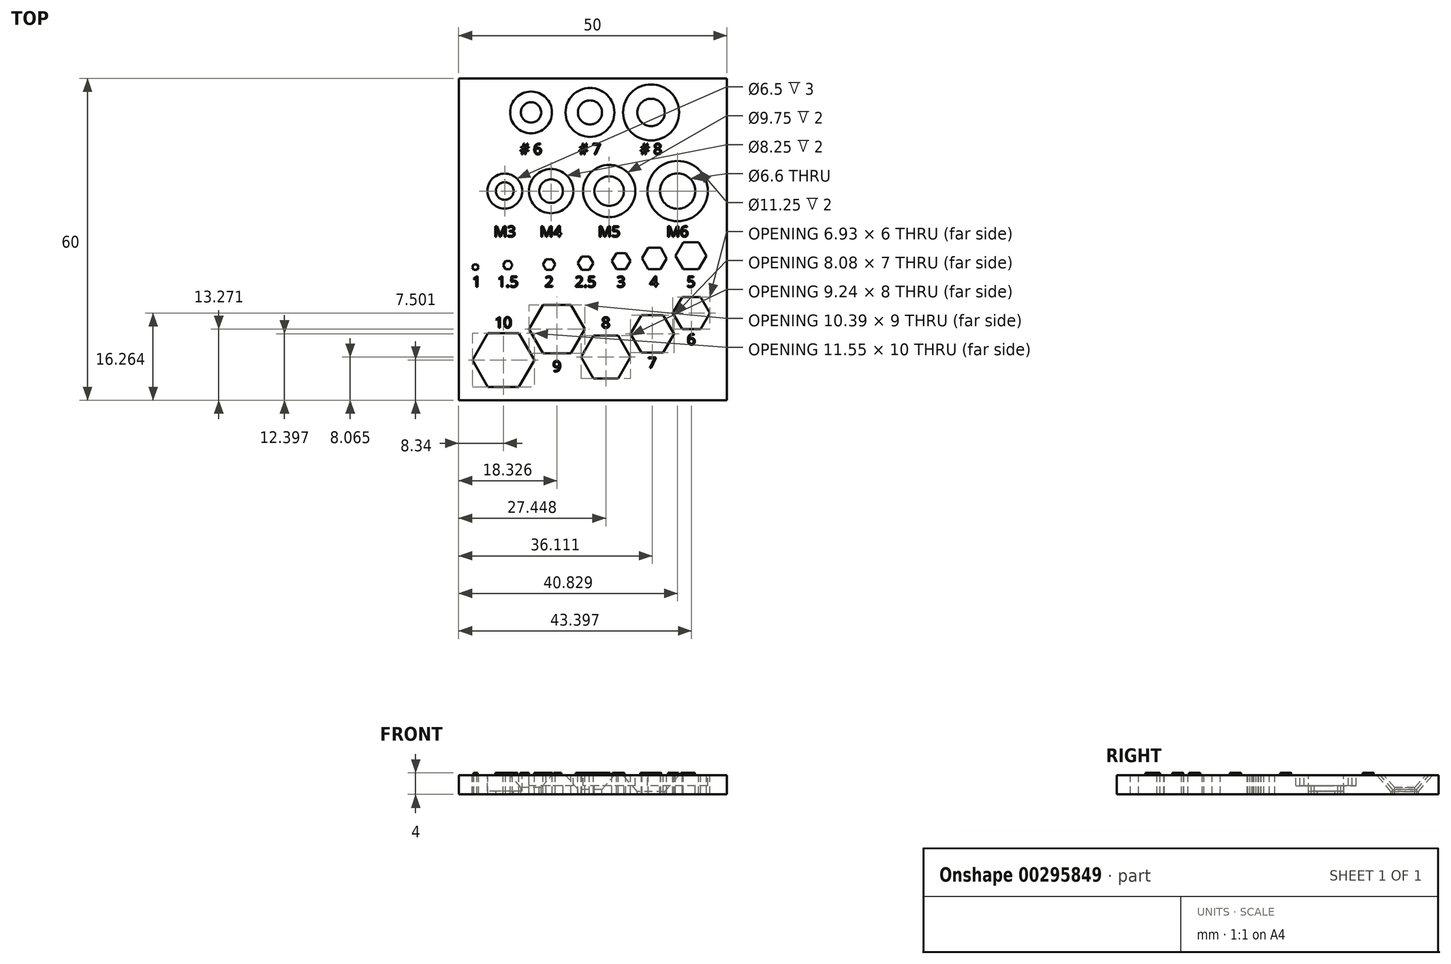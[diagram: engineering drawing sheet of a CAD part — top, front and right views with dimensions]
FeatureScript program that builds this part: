
annotation { "Feature Type Name" : "Feature", "Feature Type Description" : "" }
export const myFeature = defineFeature(function(context is Context, id is Id, definition is map)
    precondition{}
    {
        {
            var Q0;
            Q0=qCreatedBy(makeId("Top.planeOp"),FACE);
            var sketch = newSketch(context, id + "F0", { "sketchPlane" : qUnion([Q0])});
            skPoint(sketch, "E0", {"position": v(-51.98, 21.27) * mm});
            skPoint(sketch, "E1", {"position": v(-43.33, 21.27) * mm});
            skPoint(sketch, "E2", {"position": v(-32.5, 21.27) * mm});
            skPoint(sketch, "E3", {"position": v(-19.74, 21.27) * mm});
            skPoint(sketch, "E4", {"position": v(-47.08, 35.94) * mm});
            skPoint(sketch, "E5", {"position": v(-36.08, 35.94) * mm});
            skPoint(sketch, "E6", {"position": v(-24.7, 35.94) * mm});
            skCircle(sketch, "E7.cCircle", {"center": v(-57.46, 7.08) * mm, "radius": 0.5 * mm, "construction": true});
            skLineSegment(sketch, "E7.0", {"start": v(-57.75, 7.58) * mm, "end": v(-57.17, 7.58) * mm});
            skLineSegment(sketch, "E7.1", {"start": v(-57.17, 7.58) * mm, "end": v(-56.88, 7.08) * mm});
            skLineSegment(sketch, "E7.2", {"start": v(-56.88, 7.08) * mm, "end": v(-57.17, 6.58) * mm});
            skLineSegment(sketch, "E7.3", {"start": v(-57.17, 6.58) * mm, "end": v(-57.75, 6.58) * mm});
            skLineSegment(sketch, "E7.4", {"start": v(-57.75, 6.58) * mm, "end": v(-58.03, 7.08) * mm});
            skLineSegment(sketch, "E7.5", {"start": v(-58.03, 7.08) * mm, "end": v(-57.75, 7.58) * mm});
            skPoint(sketch, "E7.0.midPoint", {"position": v(-57.46, 7.58) * mm});
            skCircle(sketch, "E8.cCircle", {"center": v(-51.4, 7.45) * mm, "radius": 0.75 * mm, "construction": true});
            skLineSegment(sketch, "E8.0", {"start": v(-51.84, 8.2) * mm, "end": v(-50.97, 8.2) * mm});
            skLineSegment(sketch, "E8.1", {"start": v(-50.97, 8.2) * mm, "end": v(-50.54, 7.45) * mm});
            skLineSegment(sketch, "E8.2", {"start": v(-50.54, 7.45) * mm, "end": v(-50.97, 6.7) * mm});
            skLineSegment(sketch, "E8.3", {"start": v(-50.97, 6.7) * mm, "end": v(-51.84, 6.7) * mm});
            skLineSegment(sketch, "E8.4", {"start": v(-51.84, 6.7) * mm, "end": v(-52.27, 7.45) * mm});
            skLineSegment(sketch, "E8.5", {"start": v(-52.27, 7.45) * mm, "end": v(-51.84, 8.2) * mm});
            skPoint(sketch, "E8.0.midPoint", {"position": v(-51.4, 8.2) * mm});
            skCircle(sketch, "E9.cCircle", {"center": v(-43.7, 7.58) * mm, "radius": 1 * mm, "construction": true});
            skLineSegment(sketch, "E9.0", {"start": v(-44.28, 8.58) * mm, "end": v(-43.12, 8.58) * mm});
            skLineSegment(sketch, "E9.1", {"start": v(-43.12, 8.58) * mm, "end": v(-42.55, 7.58) * mm});
            skLineSegment(sketch, "E9.2", {"start": v(-42.55, 7.58) * mm, "end": v(-43.12, 6.58) * mm});
            skLineSegment(sketch, "E9.3", {"start": v(-43.12, 6.58) * mm, "end": v(-44.28, 6.58) * mm});
            skLineSegment(sketch, "E9.4", {"start": v(-44.28, 6.58) * mm, "end": v(-44.86, 7.58) * mm});
            skLineSegment(sketch, "E9.5", {"start": v(-44.86, 7.58) * mm, "end": v(-44.28, 8.58) * mm});
            skPoint(sketch, "E9.0.midPoint", {"position": v(-43.7, 8.58) * mm});
            skCircle(sketch, "E10.cCircle", {"center": v(-36.91, 7.83) * mm, "radius": 1.25 * mm, "construction": true});
            skLineSegment(sketch, "E10.0", {"start": v(-37.63, 9.08) * mm, "end": v(-36.2, 9.08) * mm});
            skLineSegment(sketch, "E10.1", {"start": v(-36.2, 9.08) * mm, "end": v(-35.47, 7.83) * mm});
            skLineSegment(sketch, "E10.2", {"start": v(-35.47, 7.83) * mm, "end": v(-36.2, 6.58) * mm});
            skLineSegment(sketch, "E10.3", {"start": v(-36.2, 6.58) * mm, "end": v(-37.63, 6.58) * mm});
            skLineSegment(sketch, "E10.4", {"start": v(-37.63, 6.58) * mm, "end": v(-38.36, 7.83) * mm});
            skLineSegment(sketch, "E10.5", {"start": v(-38.36, 7.83) * mm, "end": v(-37.63, 9.08) * mm});
            skPoint(sketch, "E10.0.midPoint", {"position": v(-36.91, 9.08) * mm});
            skCircle(sketch, "E11.cCircle", {"center": v(-52.23, -10.23) * mm, "radius": 5 * mm, "construction": true});
            skLineSegment(sketch, "E11.0", {"start": v(-55.12, -5.23) * mm, "end": v(-49.34, -5.23) * mm});
            skLineSegment(sketch, "E11.1", {"start": v(-49.34, -5.23) * mm, "end": v(-46.46, -10.23) * mm});
            skLineSegment(sketch, "E11.2", {"start": v(-46.46, -10.23) * mm, "end": v(-49.34, -15.23) * mm});
            skLineSegment(sketch, "E11.3", {"start": v(-49.34, -15.23) * mm, "end": v(-55.12, -15.23) * mm});
            skLineSegment(sketch, "E11.4", {"start": v(-55.12, -15.23) * mm, "end": v(-58, -10.23) * mm});
            skLineSegment(sketch, "E11.5", {"start": v(-58, -10.23) * mm, "end": v(-55.12, -5.23) * mm});
            skPoint(sketch, "E11.0.midPoint", {"position": v(-52.23, -5.23) * mm});
            skCircle(sketch, "E12.cCircle", {"center": v(-42.24, -4.46) * mm, "radius": 4.5 * mm, "construction": true});
            skLineSegment(sketch, "E12.0", {"start": v(-44.84, 0.04) * mm, "end": v(-39.65, 0.04) * mm});
            skLineSegment(sketch, "E12.1", {"start": v(-39.65, 0.04) * mm, "end": v(-37.05, -4.46) * mm});
            skLineSegment(sketch, "E12.2", {"start": v(-37.05, -4.46) * mm, "end": v(-39.65, -8.96) * mm});
            skLineSegment(sketch, "E12.3", {"start": v(-39.65, -8.96) * mm, "end": v(-44.84, -8.96) * mm});
            skLineSegment(sketch, "E12.4", {"start": v(-44.84, -8.96) * mm, "end": v(-47.44, -4.46) * mm});
            skLineSegment(sketch, "E12.5", {"start": v(-47.44, -4.46) * mm, "end": v(-44.84, 0.04) * mm});
            skPoint(sketch, "E12.0.midPoint", {"position": v(-42.24, 0.04) * mm});
            skCircle(sketch, "E13.cCircle", {"center": v(-33.12, -9.67) * mm, "radius": 4 * mm, "construction": true});
            skLineSegment(sketch, "E13.0", {"start": v(-35.43, -5.67) * mm, "end": v(-30.81, -5.67) * mm});
            skLineSegment(sketch, "E13.1", {"start": v(-30.81, -5.67) * mm, "end": v(-28.5, -9.67) * mm});
            skLineSegment(sketch, "E13.2", {"start": v(-28.5, -9.67) * mm, "end": v(-30.81, -13.67) * mm});
            skLineSegment(sketch, "E13.3", {"start": v(-30.81, -13.67) * mm, "end": v(-35.43, -13.67) * mm});
            skLineSegment(sketch, "E13.4", {"start": v(-35.43, -13.67) * mm, "end": v(-37.74, -9.67) * mm});
            skLineSegment(sketch, "E13.5", {"start": v(-37.74, -9.67) * mm, "end": v(-35.43, -5.67) * mm});
            skPoint(sketch, "E13.0.midPoint", {"position": v(-33.12, -5.67) * mm});
            skCircle(sketch, "E14.cCircle", {"center": v(-24.46, -5.33) * mm, "radius": 3.5 * mm, "construction": true});
            skLineSegment(sketch, "E14.0", {"start": v(-26.48, -1.83) * mm, "end": v(-22.44, -1.83) * mm});
            skLineSegment(sketch, "E14.1", {"start": v(-22.44, -1.83) * mm, "end": v(-20.42, -5.33) * mm});
            skLineSegment(sketch, "E14.2", {"start": v(-20.42, -5.33) * mm, "end": v(-22.44, -8.83) * mm});
            skLineSegment(sketch, "E14.3", {"start": v(-22.44, -8.83) * mm, "end": v(-26.48, -8.83) * mm});
            skLineSegment(sketch, "E14.4", {"start": v(-26.48, -8.83) * mm, "end": v(-28.5, -5.33) * mm});
            skLineSegment(sketch, "E14.5", {"start": v(-28.5, -5.33) * mm, "end": v(-26.48, -1.83) * mm});
            skPoint(sketch, "E14.0.midPoint", {"position": v(-24.46, -1.83) * mm});
            skCircle(sketch, "E15.cCircle", {"center": v(-17.17, -1.47) * mm, "radius": 3 * mm, "construction": true});
            skLineSegment(sketch, "E15.0", {"start": v(-18.9, 1.53) * mm, "end": v(-15.44, 1.53) * mm});
            skLineSegment(sketch, "E15.1", {"start": v(-15.44, 1.53) * mm, "end": v(-13.7, -1.47) * mm});
            skLineSegment(sketch, "E15.2", {"start": v(-13.7, -1.47) * mm, "end": v(-15.44, -4.47) * mm});
            skLineSegment(sketch, "E15.3", {"start": v(-15.44, -4.47) * mm, "end": v(-18.9, -4.47) * mm});
            skLineSegment(sketch, "E15.4", {"start": v(-18.9, -4.47) * mm, "end": v(-20.64, -1.47) * mm});
            skLineSegment(sketch, "E15.5", {"start": v(-20.64, -1.47) * mm, "end": v(-18.9, 1.53) * mm});
            skPoint(sketch, "E15.0.midPoint", {"position": v(-17.17, 1.53) * mm});
            skCircle(sketch, "E16.cCircle", {"center": v(-30.3, 8.2) * mm, "radius": 1.5 * mm, "construction": true});
            skLineSegment(sketch, "E16.0", {"start": v(-31.16, 9.7) * mm, "end": v(-29.43, 9.7) * mm});
            skLineSegment(sketch, "E16.1", {"start": v(-29.43, 9.7) * mm, "end": v(-28.56, 8.2) * mm});
            skLineSegment(sketch, "E16.2", {"start": v(-28.56, 8.2) * mm, "end": v(-29.43, 6.7) * mm});
            skLineSegment(sketch, "E16.3", {"start": v(-29.43, 6.7) * mm, "end": v(-31.16, 6.7) * mm});
            skLineSegment(sketch, "E16.4", {"start": v(-31.16, 6.7) * mm, "end": v(-32.02, 8.2) * mm});
            skLineSegment(sketch, "E16.5", {"start": v(-32.02, 8.2) * mm, "end": v(-31.16, 9.7) * mm});
            skPoint(sketch, "E16.0.midPoint", {"position": v(-30.3, 9.7) * mm});
            skCircle(sketch, "E17.cCircle", {"center": v(-24.08, 8.7) * mm, "radius": 2 * mm, "construction": true});
            skLineSegment(sketch, "E17.0", {"start": v(-25.22, 10.72) * mm, "end": v(-22.9, 10.7) * mm});
            skLineSegment(sketch, "E17.1", {"start": v(-22.9, 10.7) * mm, "end": v(-21.77, 8.68) * mm});
            skLineSegment(sketch, "E17.2", {"start": v(-21.77, 8.68) * mm, "end": v(-22.94, 6.7) * mm});
            skLineSegment(sketch, "E17.3", {"start": v(-22.94, 6.7) * mm, "end": v(-25.25, 6.72) * mm});
            skLineSegment(sketch, "E17.4", {"start": v(-25.25, 6.72) * mm, "end": v(-26.39, 8.73) * mm});
            skLineSegment(sketch, "E17.5", {"start": v(-26.39, 8.73) * mm, "end": v(-25.22, 10.72) * mm});
            skPoint(sketch, "E17.0.midPoint", {"position": v(-24.06, 10.7) * mm});
            skCircle(sketch, "E18.cCircle", {"center": v(-17.25, 9.2) * mm, "radius": 2.5 * mm, "construction": true});
            skLineSegment(sketch, "E18.0", {"start": v(-18.7, 11.7) * mm, "end": v(-15.8, 11.7) * mm});
            skLineSegment(sketch, "E18.1", {"start": v(-15.8, 11.7) * mm, "end": v(-14.36, 9.2) * mm});
            skLineSegment(sketch, "E18.2", {"start": v(-14.36, 9.2) * mm, "end": v(-15.8, 6.7) * mm});
            skLineSegment(sketch, "E18.3", {"start": v(-15.8, 6.7) * mm, "end": v(-18.7, 6.7) * mm});
            skLineSegment(sketch, "E18.4", {"start": v(-18.7, 6.7) * mm, "end": v(-20.13, 9.2) * mm});
            skLineSegment(sketch, "E18.5", {"start": v(-20.13, 9.2) * mm, "end": v(-18.7, 11.7) * mm});
            skPoint(sketch, "E18.0.midPoint", {"position": v(-17.25, 11.7) * mm});
            skLineSegment(sketch, "E19.bottom", {"start": v(-60.57, -17.73) * mm, "end": v(-10.57, -17.73) * mm});
            skLineSegment(sketch, "E19.top", {"start": v(-60.57, 42.27) * mm, "end": v(-10.57, 42.27) * mm});
            skLineSegment(sketch, "E19.left", {"start": v(-60.57, -17.73) * mm, "end": v(-60.57, 42.27) * mm});
            skLineSegment(sketch, "E19.right", {"start": v(-10.57, -17.73) * mm, "end": v(-10.57, 42.27) * mm});
            skSolve(sketch);
        }
        {
            var Q0;
            Q0=makeQuery(id+"F0.imprint","IMPRINT",FACE,{"disambiguationData":[TD([[makeQuery(id+"F0.imprint","IMPRINT",EDGE,{"derivedFrom":sQuery(id+"F0.wireOp",EDGE,"E7.0")}),1.0]])]});
            extrude(context, id + "F1", {"entities" : qUnion([Q0]), "oppositeDirection" : true, "depth" : 3.6 * mm});
        }
        {
            var Q0;
            Q0=sQuery(id+"F0.wireOp",VERTEX,"E0");
            var Q1;
            Q1=makeQuery(id+"F1.opExtrude","SWEPT_BODY",BODY,{"disambiguationData":[OSD([sQuery(id+"F0.wireOp",EDGE,"E7.0"),sQuery(id+"F0.wireOp",EDGE,"E7.1"),sQuery(id+"F0.wireOp",EDGE,"E7.2"),sQuery(id+"F0.wireOp",EDGE,"E7.3"),sQuery(id+"F0.wireOp",EDGE,"E7.4"),sQuery(id+"F0.wireOp",EDGE,"E7.5"),sQuery(id+"F0.wireOp",EDGE,"E8.0"),sQuery(id+"F0.wireOp",EDGE,"E8.1"),sQuery(id+"F0.wireOp",EDGE,"E8.2"),sQuery(id+"F0.wireOp",EDGE,"E8.3"),sQuery(id+"F0.wireOp",EDGE,"E8.4"),sQuery(id+"F0.wireOp",EDGE,"E8.5"),sQuery(id+"F0.wireOp",EDGE,"E9.0"),sQuery(id+"F0.wireOp",EDGE,"E9.1"),sQuery(id+"F0.wireOp",EDGE,"E9.2"),sQuery(id+"F0.wireOp",EDGE,"E9.3"),sQuery(id+"F0.wireOp",EDGE,"E9.4"),sQuery(id+"F0.wireOp",EDGE,"E9.5"),sQuery(id+"F0.wireOp",EDGE,"E10.0"),sQuery(id+"F0.wireOp",EDGE,"E10.1"),sQuery(id+"F0.wireOp",EDGE,"E10.2"),sQuery(id+"F0.wireOp",EDGE,"E10.3"),sQuery(id+"F0.wireOp",EDGE,"E10.4"),sQuery(id+"F0.wireOp",EDGE,"E10.5"),sQuery(id+"F0.wireOp",EDGE,"E11.0"),sQuery(id+"F0.wireOp",EDGE,"E11.1"),sQuery(id+"F0.wireOp",EDGE,"E11.2"),sQuery(id+"F0.wireOp",EDGE,"E11.3"),sQuery(id+"F0.wireOp",EDGE,"E11.4"),sQuery(id+"F0.wireOp",EDGE,"E11.5"),sQuery(id+"F0.wireOp",EDGE,"E12.0"),sQuery(id+"F0.wireOp",EDGE,"E12.1"),sQuery(id+"F0.wireOp",EDGE,"E12.2"),sQuery(id+"F0.wireOp",EDGE,"E12.3"),sQuery(id+"F0.wireOp",EDGE,"E12.4"),sQuery(id+"F0.wireOp",EDGE,"E12.5"),sQuery(id+"F0.wireOp",EDGE,"E13.0"),sQuery(id+"F0.wireOp",EDGE,"E13.1"),sQuery(id+"F0.wireOp",EDGE,"E13.2"),sQuery(id+"F0.wireOp",EDGE,"E13.3"),sQuery(id+"F0.wireOp",EDGE,"E13.4"),sQuery(id+"F0.wireOp",EDGE,"E13.5"),sQuery(id+"F0.wireOp",EDGE,"E14.0"),sQuery(id+"F0.wireOp",EDGE,"E14.1"),sQuery(id+"F0.wireOp",EDGE,"E14.2"),sQuery(id+"F0.wireOp",EDGE,"E14.3"),sQuery(id+"F0.wireOp",EDGE,"E14.4"),sQuery(id+"F0.wireOp",EDGE,"E14.5"),sQuery(id+"F0.wireOp",EDGE,"E15.0"),sQuery(id+"F0.wireOp",EDGE,"E15.1"),sQuery(id+"F0.wireOp",EDGE,"E15.2"),sQuery(id+"F0.wireOp",EDGE,"E15.3"),sQuery(id+"F0.wireOp",EDGE,"E15.4"),sQuery(id+"F0.wireOp",EDGE,"E15.5"),sQuery(id+"F0.wireOp",EDGE,"E16.0"),sQuery(id+"F0.wireOp",EDGE,"E16.1"),sQuery(id+"F0.wireOp",EDGE,"E16.2"),sQuery(id+"F0.wireOp",EDGE,"E16.3"),sQuery(id+"F0.wireOp",EDGE,"E16.4"),sQuery(id+"F0.wireOp",EDGE,"E16.5"),sQuery(id+"F0.wireOp",EDGE,"E17.0"),sQuery(id+"F0.wireOp",EDGE,"E17.1"),sQuery(id+"F0.wireOp",EDGE,"E17.2"),sQuery(id+"F0.wireOp",EDGE,"E17.3"),sQuery(id+"F0.wireOp",EDGE,"E17.4"),sQuery(id+"F0.wireOp",EDGE,"E17.5"),sQuery(id+"F0.wireOp",EDGE,"E18.0"),sQuery(id+"F0.wireOp",EDGE,"E18.1"),sQuery(id+"F0.wireOp",EDGE,"E18.2"),sQuery(id+"F0.wireOp",EDGE,"E18.3"),sQuery(id+"F0.wireOp",EDGE,"E18.4"),sQuery(id+"F0.wireOp",EDGE,"E18.5"),sQuery(id+"F0.wireOp",EDGE,"E19.bottom"),sQuery(id+"F0.wireOp",EDGE,"E19.top"),sQuery(id+"F0.wireOp",EDGE,"E19.left"),sQuery(id+"F0.wireOp",EDGE,"E19.right")])]});
            hole(context, id + "F2", {"style" : HoleStyle.C_BORE, "endStyle" : HoleEndStyle.THROUGH, "standardTappedOrClearance" : lookupTablePath({ "standard" : "ISO", "fit" : "Normal", "size" : "M3", "type" : "Clearance" }), "standardBlindInLast" : lookupTablePath({ "fit" : "Standard", "standard" : "ISO", "size" : "M3", "type" : "Clearance" }), "holeDiameter" : 3.3 * mm, "cBoreDiameter" : 6.5 * mm, "cBoreDepth" : 3 * mm, "tappedDepth" : 12.7 * mm, "tapClearance" : 3, "locations" : qUnion([Q0]), "scope" : qUnion([Q1])});
        }
        {
            var Q0;
            Q0=sQuery(id+"F0.wireOp",VERTEX,"E2");
            var Q1;
            Q1=makeQuery(id+"F1.opExtrude","SWEPT_BODY",BODY,{"disambiguationData":[OSD([sQuery(id+"F0.wireOp",EDGE,"E7.0"),sQuery(id+"F0.wireOp",EDGE,"E7.1"),sQuery(id+"F0.wireOp",EDGE,"E7.2"),sQuery(id+"F0.wireOp",EDGE,"E7.3"),sQuery(id+"F0.wireOp",EDGE,"E7.4"),sQuery(id+"F0.wireOp",EDGE,"E7.5"),sQuery(id+"F0.wireOp",EDGE,"E8.0"),sQuery(id+"F0.wireOp",EDGE,"E8.1"),sQuery(id+"F0.wireOp",EDGE,"E8.2"),sQuery(id+"F0.wireOp",EDGE,"E8.3"),sQuery(id+"F0.wireOp",EDGE,"E8.4"),sQuery(id+"F0.wireOp",EDGE,"E8.5"),sQuery(id+"F0.wireOp",EDGE,"E9.0"),sQuery(id+"F0.wireOp",EDGE,"E9.1"),sQuery(id+"F0.wireOp",EDGE,"E9.2"),sQuery(id+"F0.wireOp",EDGE,"E9.3"),sQuery(id+"F0.wireOp",EDGE,"E9.4"),sQuery(id+"F0.wireOp",EDGE,"E9.5"),sQuery(id+"F0.wireOp",EDGE,"E10.0"),sQuery(id+"F0.wireOp",EDGE,"E10.1"),sQuery(id+"F0.wireOp",EDGE,"E10.2"),sQuery(id+"F0.wireOp",EDGE,"E10.3"),sQuery(id+"F0.wireOp",EDGE,"E10.4"),sQuery(id+"F0.wireOp",EDGE,"E10.5"),sQuery(id+"F0.wireOp",EDGE,"E11.0"),sQuery(id+"F0.wireOp",EDGE,"E11.1"),sQuery(id+"F0.wireOp",EDGE,"E11.2"),sQuery(id+"F0.wireOp",EDGE,"E11.3"),sQuery(id+"F0.wireOp",EDGE,"E11.4"),sQuery(id+"F0.wireOp",EDGE,"E11.5"),sQuery(id+"F0.wireOp",EDGE,"E12.0"),sQuery(id+"F0.wireOp",EDGE,"E12.1"),sQuery(id+"F0.wireOp",EDGE,"E12.2"),sQuery(id+"F0.wireOp",EDGE,"E12.3"),sQuery(id+"F0.wireOp",EDGE,"E12.4"),sQuery(id+"F0.wireOp",EDGE,"E12.5"),sQuery(id+"F0.wireOp",EDGE,"E13.0"),sQuery(id+"F0.wireOp",EDGE,"E13.1"),sQuery(id+"F0.wireOp",EDGE,"E13.2"),sQuery(id+"F0.wireOp",EDGE,"E13.3"),sQuery(id+"F0.wireOp",EDGE,"E13.4"),sQuery(id+"F0.wireOp",EDGE,"E13.5"),sQuery(id+"F0.wireOp",EDGE,"E14.0"),sQuery(id+"F0.wireOp",EDGE,"E14.1"),sQuery(id+"F0.wireOp",EDGE,"E14.2"),sQuery(id+"F0.wireOp",EDGE,"E14.3"),sQuery(id+"F0.wireOp",EDGE,"E14.4"),sQuery(id+"F0.wireOp",EDGE,"E14.5"),sQuery(id+"F0.wireOp",EDGE,"E15.0"),sQuery(id+"F0.wireOp",EDGE,"E15.1"),sQuery(id+"F0.wireOp",EDGE,"E15.2"),sQuery(id+"F0.wireOp",EDGE,"E15.3"),sQuery(id+"F0.wireOp",EDGE,"E15.4"),sQuery(id+"F0.wireOp",EDGE,"E15.5"),sQuery(id+"F0.wireOp",EDGE,"E16.0"),sQuery(id+"F0.wireOp",EDGE,"E16.1"),sQuery(id+"F0.wireOp",EDGE,"E16.2"),sQuery(id+"F0.wireOp",EDGE,"E16.3"),sQuery(id+"F0.wireOp",EDGE,"E16.4"),sQuery(id+"F0.wireOp",EDGE,"E16.5"),sQuery(id+"F0.wireOp",EDGE,"E17.0"),sQuery(id+"F0.wireOp",EDGE,"E17.1"),sQuery(id+"F0.wireOp",EDGE,"E17.2"),sQuery(id+"F0.wireOp",EDGE,"E17.3"),sQuery(id+"F0.wireOp",EDGE,"E17.4"),sQuery(id+"F0.wireOp",EDGE,"E17.5"),sQuery(id+"F0.wireOp",EDGE,"E18.0"),sQuery(id+"F0.wireOp",EDGE,"E18.1"),sQuery(id+"F0.wireOp",EDGE,"E18.2"),sQuery(id+"F0.wireOp",EDGE,"E18.3"),sQuery(id+"F0.wireOp",EDGE,"E18.4"),sQuery(id+"F0.wireOp",EDGE,"E18.5"),sQuery(id+"F0.wireOp",EDGE,"E19.bottom"),sQuery(id+"F0.wireOp",EDGE,"E19.top"),sQuery(id+"F0.wireOp",EDGE,"E19.left"),sQuery(id+"F0.wireOp",EDGE,"E19.right")])]});
            hole(context, id + "F3", {"style" : HoleStyle.C_BORE, "endStyle" : HoleEndStyle.THROUGH, "holeDiameter" : 5.5 * mm, "cBoreDiameter" : 9.75 * mm, "cBoreDepth" : 2 * mm, "tappedDepth" : 12.7 * mm, "tapClearance" : 3, "locations" : qUnion([Q0]), "scope" : qUnion([Q1])});
        }
        {
            var Q0;
            Q0=sQuery(id+"F0.wireOp",VERTEX,"E1");
            var Q1;
            Q1=makeQuery(id+"F1.opExtrude","SWEPT_BODY",BODY,{"disambiguationData":[OSD([sQuery(id+"F0.wireOp",EDGE,"E7.0"),sQuery(id+"F0.wireOp",EDGE,"E7.1"),sQuery(id+"F0.wireOp",EDGE,"E7.2"),sQuery(id+"F0.wireOp",EDGE,"E7.3"),sQuery(id+"F0.wireOp",EDGE,"E7.4"),sQuery(id+"F0.wireOp",EDGE,"E7.5"),sQuery(id+"F0.wireOp",EDGE,"E8.0"),sQuery(id+"F0.wireOp",EDGE,"E8.1"),sQuery(id+"F0.wireOp",EDGE,"E8.2"),sQuery(id+"F0.wireOp",EDGE,"E8.3"),sQuery(id+"F0.wireOp",EDGE,"E8.4"),sQuery(id+"F0.wireOp",EDGE,"E8.5"),sQuery(id+"F0.wireOp",EDGE,"E9.0"),sQuery(id+"F0.wireOp",EDGE,"E9.1"),sQuery(id+"F0.wireOp",EDGE,"E9.2"),sQuery(id+"F0.wireOp",EDGE,"E9.3"),sQuery(id+"F0.wireOp",EDGE,"E9.4"),sQuery(id+"F0.wireOp",EDGE,"E9.5"),sQuery(id+"F0.wireOp",EDGE,"E10.0"),sQuery(id+"F0.wireOp",EDGE,"E10.1"),sQuery(id+"F0.wireOp",EDGE,"E10.2"),sQuery(id+"F0.wireOp",EDGE,"E10.3"),sQuery(id+"F0.wireOp",EDGE,"E10.4"),sQuery(id+"F0.wireOp",EDGE,"E10.5"),sQuery(id+"F0.wireOp",EDGE,"E11.0"),sQuery(id+"F0.wireOp",EDGE,"E11.1"),sQuery(id+"F0.wireOp",EDGE,"E11.2"),sQuery(id+"F0.wireOp",EDGE,"E11.3"),sQuery(id+"F0.wireOp",EDGE,"E11.4"),sQuery(id+"F0.wireOp",EDGE,"E11.5"),sQuery(id+"F0.wireOp",EDGE,"E12.0"),sQuery(id+"F0.wireOp",EDGE,"E12.1"),sQuery(id+"F0.wireOp",EDGE,"E12.2"),sQuery(id+"F0.wireOp",EDGE,"E12.3"),sQuery(id+"F0.wireOp",EDGE,"E12.4"),sQuery(id+"F0.wireOp",EDGE,"E12.5"),sQuery(id+"F0.wireOp",EDGE,"E13.0"),sQuery(id+"F0.wireOp",EDGE,"E13.1"),sQuery(id+"F0.wireOp",EDGE,"E13.2"),sQuery(id+"F0.wireOp",EDGE,"E13.3"),sQuery(id+"F0.wireOp",EDGE,"E13.4"),sQuery(id+"F0.wireOp",EDGE,"E13.5"),sQuery(id+"F0.wireOp",EDGE,"E14.0"),sQuery(id+"F0.wireOp",EDGE,"E14.1"),sQuery(id+"F0.wireOp",EDGE,"E14.2"),sQuery(id+"F0.wireOp",EDGE,"E14.3"),sQuery(id+"F0.wireOp",EDGE,"E14.4"),sQuery(id+"F0.wireOp",EDGE,"E14.5"),sQuery(id+"F0.wireOp",EDGE,"E15.0"),sQuery(id+"F0.wireOp",EDGE,"E15.1"),sQuery(id+"F0.wireOp",EDGE,"E15.2"),sQuery(id+"F0.wireOp",EDGE,"E15.3"),sQuery(id+"F0.wireOp",EDGE,"E15.4"),sQuery(id+"F0.wireOp",EDGE,"E15.5"),sQuery(id+"F0.wireOp",EDGE,"E16.0"),sQuery(id+"F0.wireOp",EDGE,"E16.1"),sQuery(id+"F0.wireOp",EDGE,"E16.2"),sQuery(id+"F0.wireOp",EDGE,"E16.3"),sQuery(id+"F0.wireOp",EDGE,"E16.4"),sQuery(id+"F0.wireOp",EDGE,"E16.5"),sQuery(id+"F0.wireOp",EDGE,"E17.0"),sQuery(id+"F0.wireOp",EDGE,"E17.1"),sQuery(id+"F0.wireOp",EDGE,"E17.2"),sQuery(id+"F0.wireOp",EDGE,"E17.3"),sQuery(id+"F0.wireOp",EDGE,"E17.4"),sQuery(id+"F0.wireOp",EDGE,"E17.5"),sQuery(id+"F0.wireOp",EDGE,"E18.0"),sQuery(id+"F0.wireOp",EDGE,"E18.1"),sQuery(id+"F0.wireOp",EDGE,"E18.2"),sQuery(id+"F0.wireOp",EDGE,"E18.3"),sQuery(id+"F0.wireOp",EDGE,"E18.4"),sQuery(id+"F0.wireOp",EDGE,"E18.5"),sQuery(id+"F0.wireOp",EDGE,"E19.bottom"),sQuery(id+"F0.wireOp",EDGE,"E19.top"),sQuery(id+"F0.wireOp",EDGE,"E19.left"),sQuery(id+"F0.wireOp",EDGE,"E19.right")])]});
            hole(context, id + "F4", {"style" : HoleStyle.C_BORE, "endStyle" : HoleEndStyle.THROUGH, "holeDiameter" : 4.4 * mm, "cBoreDiameter" : 8.25 * mm, "cBoreDepth" : 2 * mm, "tappedDepth" : 12.7 * mm, "tapClearance" : 3, "locations" : qUnion([Q0]), "scope" : qUnion([Q1])});
        }
        {
            var Q0;
            Q0=sQuery(id+"F0.wireOp",VERTEX,"E3");
            var Q1;
            Q1=makeQuery(id+"F1.opExtrude","SWEPT_BODY",BODY,{"disambiguationData":[OSD([sQuery(id+"F0.wireOp",EDGE,"E7.0"),sQuery(id+"F0.wireOp",EDGE,"E7.1"),sQuery(id+"F0.wireOp",EDGE,"E7.2"),sQuery(id+"F0.wireOp",EDGE,"E7.3"),sQuery(id+"F0.wireOp",EDGE,"E7.4"),sQuery(id+"F0.wireOp",EDGE,"E7.5"),sQuery(id+"F0.wireOp",EDGE,"E8.0"),sQuery(id+"F0.wireOp",EDGE,"E8.1"),sQuery(id+"F0.wireOp",EDGE,"E8.2"),sQuery(id+"F0.wireOp",EDGE,"E8.3"),sQuery(id+"F0.wireOp",EDGE,"E8.4"),sQuery(id+"F0.wireOp",EDGE,"E8.5"),sQuery(id+"F0.wireOp",EDGE,"E9.0"),sQuery(id+"F0.wireOp",EDGE,"E9.1"),sQuery(id+"F0.wireOp",EDGE,"E9.2"),sQuery(id+"F0.wireOp",EDGE,"E9.3"),sQuery(id+"F0.wireOp",EDGE,"E9.4"),sQuery(id+"F0.wireOp",EDGE,"E9.5"),sQuery(id+"F0.wireOp",EDGE,"E10.0"),sQuery(id+"F0.wireOp",EDGE,"E10.1"),sQuery(id+"F0.wireOp",EDGE,"E10.2"),sQuery(id+"F0.wireOp",EDGE,"E10.3"),sQuery(id+"F0.wireOp",EDGE,"E10.4"),sQuery(id+"F0.wireOp",EDGE,"E10.5"),sQuery(id+"F0.wireOp",EDGE,"E11.0"),sQuery(id+"F0.wireOp",EDGE,"E11.1"),sQuery(id+"F0.wireOp",EDGE,"E11.2"),sQuery(id+"F0.wireOp",EDGE,"E11.3"),sQuery(id+"F0.wireOp",EDGE,"E11.4"),sQuery(id+"F0.wireOp",EDGE,"E11.5"),sQuery(id+"F0.wireOp",EDGE,"E12.0"),sQuery(id+"F0.wireOp",EDGE,"E12.1"),sQuery(id+"F0.wireOp",EDGE,"E12.2"),sQuery(id+"F0.wireOp",EDGE,"E12.3"),sQuery(id+"F0.wireOp",EDGE,"E12.4"),sQuery(id+"F0.wireOp",EDGE,"E12.5"),sQuery(id+"F0.wireOp",EDGE,"E13.0"),sQuery(id+"F0.wireOp",EDGE,"E13.1"),sQuery(id+"F0.wireOp",EDGE,"E13.2"),sQuery(id+"F0.wireOp",EDGE,"E13.3"),sQuery(id+"F0.wireOp",EDGE,"E13.4"),sQuery(id+"F0.wireOp",EDGE,"E13.5"),sQuery(id+"F0.wireOp",EDGE,"E14.0"),sQuery(id+"F0.wireOp",EDGE,"E14.1"),sQuery(id+"F0.wireOp",EDGE,"E14.2"),sQuery(id+"F0.wireOp",EDGE,"E14.3"),sQuery(id+"F0.wireOp",EDGE,"E14.4"),sQuery(id+"F0.wireOp",EDGE,"E14.5"),sQuery(id+"F0.wireOp",EDGE,"E15.0"),sQuery(id+"F0.wireOp",EDGE,"E15.1"),sQuery(id+"F0.wireOp",EDGE,"E15.2"),sQuery(id+"F0.wireOp",EDGE,"E15.3"),sQuery(id+"F0.wireOp",EDGE,"E15.4"),sQuery(id+"F0.wireOp",EDGE,"E15.5"),sQuery(id+"F0.wireOp",EDGE,"E16.0"),sQuery(id+"F0.wireOp",EDGE,"E16.1"),sQuery(id+"F0.wireOp",EDGE,"E16.2"),sQuery(id+"F0.wireOp",EDGE,"E16.3"),sQuery(id+"F0.wireOp",EDGE,"E16.4"),sQuery(id+"F0.wireOp",EDGE,"E16.5"),sQuery(id+"F0.wireOp",EDGE,"E17.0"),sQuery(id+"F0.wireOp",EDGE,"E17.1"),sQuery(id+"F0.wireOp",EDGE,"E17.2"),sQuery(id+"F0.wireOp",EDGE,"E17.3"),sQuery(id+"F0.wireOp",EDGE,"E17.4"),sQuery(id+"F0.wireOp",EDGE,"E17.5"),sQuery(id+"F0.wireOp",EDGE,"E18.0"),sQuery(id+"F0.wireOp",EDGE,"E18.1"),sQuery(id+"F0.wireOp",EDGE,"E18.2"),sQuery(id+"F0.wireOp",EDGE,"E18.3"),sQuery(id+"F0.wireOp",EDGE,"E18.4"),sQuery(id+"F0.wireOp",EDGE,"E18.5"),sQuery(id+"F0.wireOp",EDGE,"E19.bottom"),sQuery(id+"F0.wireOp",EDGE,"E19.top"),sQuery(id+"F0.wireOp",EDGE,"E19.left"),sQuery(id+"F0.wireOp",EDGE,"E19.right")])]});
            hole(context, id + "F5", {"style" : HoleStyle.C_BORE, "endStyle" : HoleEndStyle.THROUGH, "holeDiameter" : 6.6 * mm, "cBoreDiameter" : 11.25 * mm, "cBoreDepth" : 2 * mm, "tappedDepth" : 12.7 * mm, "tapClearance" : 3, "locations" : qUnion([Q0]), "scope" : qUnion([Q1])});
        }
        {
            var Q0;
            Q0=sQuery(id+"F0.wireOp",VERTEX,"E4");
            var Q1;
            Q1=makeQuery(id+"F1.opExtrude","SWEPT_BODY",BODY,{"disambiguationData":[OSD([sQuery(id+"F0.wireOp",EDGE,"E7.0"),sQuery(id+"F0.wireOp",EDGE,"E7.1"),sQuery(id+"F0.wireOp",EDGE,"E7.2"),sQuery(id+"F0.wireOp",EDGE,"E7.3"),sQuery(id+"F0.wireOp",EDGE,"E7.4"),sQuery(id+"F0.wireOp",EDGE,"E7.5"),sQuery(id+"F0.wireOp",EDGE,"E8.0"),sQuery(id+"F0.wireOp",EDGE,"E8.1"),sQuery(id+"F0.wireOp",EDGE,"E8.2"),sQuery(id+"F0.wireOp",EDGE,"E8.3"),sQuery(id+"F0.wireOp",EDGE,"E8.4"),sQuery(id+"F0.wireOp",EDGE,"E8.5"),sQuery(id+"F0.wireOp",EDGE,"E9.0"),sQuery(id+"F0.wireOp",EDGE,"E9.1"),sQuery(id+"F0.wireOp",EDGE,"E9.2"),sQuery(id+"F0.wireOp",EDGE,"E9.3"),sQuery(id+"F0.wireOp",EDGE,"E9.4"),sQuery(id+"F0.wireOp",EDGE,"E9.5"),sQuery(id+"F0.wireOp",EDGE,"E10.0"),sQuery(id+"F0.wireOp",EDGE,"E10.1"),sQuery(id+"F0.wireOp",EDGE,"E10.2"),sQuery(id+"F0.wireOp",EDGE,"E10.3"),sQuery(id+"F0.wireOp",EDGE,"E10.4"),sQuery(id+"F0.wireOp",EDGE,"E10.5"),sQuery(id+"F0.wireOp",EDGE,"E11.0"),sQuery(id+"F0.wireOp",EDGE,"E11.1"),sQuery(id+"F0.wireOp",EDGE,"E11.2"),sQuery(id+"F0.wireOp",EDGE,"E11.3"),sQuery(id+"F0.wireOp",EDGE,"E11.4"),sQuery(id+"F0.wireOp",EDGE,"E11.5"),sQuery(id+"F0.wireOp",EDGE,"E12.0"),sQuery(id+"F0.wireOp",EDGE,"E12.1"),sQuery(id+"F0.wireOp",EDGE,"E12.2"),sQuery(id+"F0.wireOp",EDGE,"E12.3"),sQuery(id+"F0.wireOp",EDGE,"E12.4"),sQuery(id+"F0.wireOp",EDGE,"E12.5"),sQuery(id+"F0.wireOp",EDGE,"E13.0"),sQuery(id+"F0.wireOp",EDGE,"E13.1"),sQuery(id+"F0.wireOp",EDGE,"E13.2"),sQuery(id+"F0.wireOp",EDGE,"E13.3"),sQuery(id+"F0.wireOp",EDGE,"E13.4"),sQuery(id+"F0.wireOp",EDGE,"E13.5"),sQuery(id+"F0.wireOp",EDGE,"E14.0"),sQuery(id+"F0.wireOp",EDGE,"E14.1"),sQuery(id+"F0.wireOp",EDGE,"E14.2"),sQuery(id+"F0.wireOp",EDGE,"E14.3"),sQuery(id+"F0.wireOp",EDGE,"E14.4"),sQuery(id+"F0.wireOp",EDGE,"E14.5"),sQuery(id+"F0.wireOp",EDGE,"E15.0"),sQuery(id+"F0.wireOp",EDGE,"E15.1"),sQuery(id+"F0.wireOp",EDGE,"E15.2"),sQuery(id+"F0.wireOp",EDGE,"E15.3"),sQuery(id+"F0.wireOp",EDGE,"E15.4"),sQuery(id+"F0.wireOp",EDGE,"E15.5"),sQuery(id+"F0.wireOp",EDGE,"E16.0"),sQuery(id+"F0.wireOp",EDGE,"E16.1"),sQuery(id+"F0.wireOp",EDGE,"E16.2"),sQuery(id+"F0.wireOp",EDGE,"E16.3"),sQuery(id+"F0.wireOp",EDGE,"E16.4"),sQuery(id+"F0.wireOp",EDGE,"E16.5"),sQuery(id+"F0.wireOp",EDGE,"E17.0"),sQuery(id+"F0.wireOp",EDGE,"E17.1"),sQuery(id+"F0.wireOp",EDGE,"E17.2"),sQuery(id+"F0.wireOp",EDGE,"E17.3"),sQuery(id+"F0.wireOp",EDGE,"E17.4"),sQuery(id+"F0.wireOp",EDGE,"E17.5"),sQuery(id+"F0.wireOp",EDGE,"E18.0"),sQuery(id+"F0.wireOp",EDGE,"E18.1"),sQuery(id+"F0.wireOp",EDGE,"E18.2"),sQuery(id+"F0.wireOp",EDGE,"E18.3"),sQuery(id+"F0.wireOp",EDGE,"E18.4"),sQuery(id+"F0.wireOp",EDGE,"E18.5"),sQuery(id+"F0.wireOp",EDGE,"E19.bottom"),sQuery(id+"F0.wireOp",EDGE,"E19.top"),sQuery(id+"F0.wireOp",EDGE,"E19.left"),sQuery(id+"F0.wireOp",EDGE,"E19.right")])]});
            hole(context, id + "F6", {"style" : HoleStyle.C_SINK, "endStyle" : HoleEndStyle.THROUGH, "standardTappedOrClearance" : lookupTablePath({ "standard" : "ANSI", "fit" : "Normal (ASME)", "size" : "#6", "type" : "Clearance" }), "standardBlindInLast" : lookupTablePath({ "fit" : "Free", "standard" : "ANSI", "size" : "#6", "type" : "Clearance" }), "holeDiameter" : 3.8 * mm, "cSinkDiameter" : 7.8 * mm, "cSinkAngle" : 82 * degree, "tappedDepth" : 12.7 * mm, "tapClearance" : 3, "locations" : qUnion([Q0]), "scope" : qUnion([Q1])});
        }
        {
            var Q0;
            Q0=sQuery(id+"F0.wireOp",VERTEX,"E5");
            var Q1;
            Q1=makeQuery(id+"F1.opExtrude","SWEPT_BODY",BODY,{"disambiguationData":[OSD([sQuery(id+"F0.wireOp",EDGE,"E7.0"),sQuery(id+"F0.wireOp",EDGE,"E7.1"),sQuery(id+"F0.wireOp",EDGE,"E7.2"),sQuery(id+"F0.wireOp",EDGE,"E7.3"),sQuery(id+"F0.wireOp",EDGE,"E7.4"),sQuery(id+"F0.wireOp",EDGE,"E7.5"),sQuery(id+"F0.wireOp",EDGE,"E8.0"),sQuery(id+"F0.wireOp",EDGE,"E8.1"),sQuery(id+"F0.wireOp",EDGE,"E8.2"),sQuery(id+"F0.wireOp",EDGE,"E8.3"),sQuery(id+"F0.wireOp",EDGE,"E8.4"),sQuery(id+"F0.wireOp",EDGE,"E8.5"),sQuery(id+"F0.wireOp",EDGE,"E9.0"),sQuery(id+"F0.wireOp",EDGE,"E9.1"),sQuery(id+"F0.wireOp",EDGE,"E9.2"),sQuery(id+"F0.wireOp",EDGE,"E9.3"),sQuery(id+"F0.wireOp",EDGE,"E9.4"),sQuery(id+"F0.wireOp",EDGE,"E9.5"),sQuery(id+"F0.wireOp",EDGE,"E10.0"),sQuery(id+"F0.wireOp",EDGE,"E10.1"),sQuery(id+"F0.wireOp",EDGE,"E10.2"),sQuery(id+"F0.wireOp",EDGE,"E10.3"),sQuery(id+"F0.wireOp",EDGE,"E10.4"),sQuery(id+"F0.wireOp",EDGE,"E10.5"),sQuery(id+"F0.wireOp",EDGE,"E11.0"),sQuery(id+"F0.wireOp",EDGE,"E11.1"),sQuery(id+"F0.wireOp",EDGE,"E11.2"),sQuery(id+"F0.wireOp",EDGE,"E11.3"),sQuery(id+"F0.wireOp",EDGE,"E11.4"),sQuery(id+"F0.wireOp",EDGE,"E11.5"),sQuery(id+"F0.wireOp",EDGE,"E12.0"),sQuery(id+"F0.wireOp",EDGE,"E12.1"),sQuery(id+"F0.wireOp",EDGE,"E12.2"),sQuery(id+"F0.wireOp",EDGE,"E12.3"),sQuery(id+"F0.wireOp",EDGE,"E12.4"),sQuery(id+"F0.wireOp",EDGE,"E12.5"),sQuery(id+"F0.wireOp",EDGE,"E13.0"),sQuery(id+"F0.wireOp",EDGE,"E13.1"),sQuery(id+"F0.wireOp",EDGE,"E13.2"),sQuery(id+"F0.wireOp",EDGE,"E13.3"),sQuery(id+"F0.wireOp",EDGE,"E13.4"),sQuery(id+"F0.wireOp",EDGE,"E13.5"),sQuery(id+"F0.wireOp",EDGE,"E14.0"),sQuery(id+"F0.wireOp",EDGE,"E14.1"),sQuery(id+"F0.wireOp",EDGE,"E14.2"),sQuery(id+"F0.wireOp",EDGE,"E14.3"),sQuery(id+"F0.wireOp",EDGE,"E14.4"),sQuery(id+"F0.wireOp",EDGE,"E14.5"),sQuery(id+"F0.wireOp",EDGE,"E15.0"),sQuery(id+"F0.wireOp",EDGE,"E15.1"),sQuery(id+"F0.wireOp",EDGE,"E15.2"),sQuery(id+"F0.wireOp",EDGE,"E15.3"),sQuery(id+"F0.wireOp",EDGE,"E15.4"),sQuery(id+"F0.wireOp",EDGE,"E15.5"),sQuery(id+"F0.wireOp",EDGE,"E16.0"),sQuery(id+"F0.wireOp",EDGE,"E16.1"),sQuery(id+"F0.wireOp",EDGE,"E16.2"),sQuery(id+"F0.wireOp",EDGE,"E16.3"),sQuery(id+"F0.wireOp",EDGE,"E16.4"),sQuery(id+"F0.wireOp",EDGE,"E16.5"),sQuery(id+"F0.wireOp",EDGE,"E17.0"),sQuery(id+"F0.wireOp",EDGE,"E17.1"),sQuery(id+"F0.wireOp",EDGE,"E17.2"),sQuery(id+"F0.wireOp",EDGE,"E17.3"),sQuery(id+"F0.wireOp",EDGE,"E17.4"),sQuery(id+"F0.wireOp",EDGE,"E17.5"),sQuery(id+"F0.wireOp",EDGE,"E18.0"),sQuery(id+"F0.wireOp",EDGE,"E18.1"),sQuery(id+"F0.wireOp",EDGE,"E18.2"),sQuery(id+"F0.wireOp",EDGE,"E18.3"),sQuery(id+"F0.wireOp",EDGE,"E18.4"),sQuery(id+"F0.wireOp",EDGE,"E18.5"),sQuery(id+"F0.wireOp",EDGE,"E19.bottom"),sQuery(id+"F0.wireOp",EDGE,"E19.top"),sQuery(id+"F0.wireOp",EDGE,"E19.left"),sQuery(id+"F0.wireOp",EDGE,"E19.right")])]});
            hole(context, id + "F7", {"style" : HoleStyle.C_SINK, "endStyle" : HoleEndStyle.THROUGH, "standardTappedOrClearance" : lookupTablePath({ "standard" : "ANSI", "fit" : "Normal (ASME)", "size" : "#8", "type" : "Clearance" }), "standardBlindInLast" : lookupTablePath({ "fit" : "Free", "standard" : "ANSI", "size" : "#8", "type" : "Clearance" }), "holeDiameter" : 4.5 * mm, "cSinkDiameter" : 9.12 * mm, "cSinkAngle" : 82 * degree, "tappedDepth" : 12.7 * mm, "tapClearance" : 3, "locations" : qUnion([Q0]), "scope" : qUnion([Q1])});
        }
        {
            var Q0;
            Q0=sQuery(id+"F0.wireOp",VERTEX,"E6");
            var Q1;
            Q1=makeQuery(id+"F1.opExtrude","SWEPT_BODY",BODY,{"disambiguationData":[OSD([sQuery(id+"F0.wireOp",EDGE,"E7.0"),sQuery(id+"F0.wireOp",EDGE,"E7.1"),sQuery(id+"F0.wireOp",EDGE,"E7.2"),sQuery(id+"F0.wireOp",EDGE,"E7.3"),sQuery(id+"F0.wireOp",EDGE,"E7.4"),sQuery(id+"F0.wireOp",EDGE,"E7.5"),sQuery(id+"F0.wireOp",EDGE,"E8.0"),sQuery(id+"F0.wireOp",EDGE,"E8.1"),sQuery(id+"F0.wireOp",EDGE,"E8.2"),sQuery(id+"F0.wireOp",EDGE,"E8.3"),sQuery(id+"F0.wireOp",EDGE,"E8.4"),sQuery(id+"F0.wireOp",EDGE,"E8.5"),sQuery(id+"F0.wireOp",EDGE,"E9.0"),sQuery(id+"F0.wireOp",EDGE,"E9.1"),sQuery(id+"F0.wireOp",EDGE,"E9.2"),sQuery(id+"F0.wireOp",EDGE,"E9.3"),sQuery(id+"F0.wireOp",EDGE,"E9.4"),sQuery(id+"F0.wireOp",EDGE,"E9.5"),sQuery(id+"F0.wireOp",EDGE,"E10.0"),sQuery(id+"F0.wireOp",EDGE,"E10.1"),sQuery(id+"F0.wireOp",EDGE,"E10.2"),sQuery(id+"F0.wireOp",EDGE,"E10.3"),sQuery(id+"F0.wireOp",EDGE,"E10.4"),sQuery(id+"F0.wireOp",EDGE,"E10.5"),sQuery(id+"F0.wireOp",EDGE,"E11.0"),sQuery(id+"F0.wireOp",EDGE,"E11.1"),sQuery(id+"F0.wireOp",EDGE,"E11.2"),sQuery(id+"F0.wireOp",EDGE,"E11.3"),sQuery(id+"F0.wireOp",EDGE,"E11.4"),sQuery(id+"F0.wireOp",EDGE,"E11.5"),sQuery(id+"F0.wireOp",EDGE,"E12.0"),sQuery(id+"F0.wireOp",EDGE,"E12.1"),sQuery(id+"F0.wireOp",EDGE,"E12.2"),sQuery(id+"F0.wireOp",EDGE,"E12.3"),sQuery(id+"F0.wireOp",EDGE,"E12.4"),sQuery(id+"F0.wireOp",EDGE,"E12.5"),sQuery(id+"F0.wireOp",EDGE,"E13.0"),sQuery(id+"F0.wireOp",EDGE,"E13.1"),sQuery(id+"F0.wireOp",EDGE,"E13.2"),sQuery(id+"F0.wireOp",EDGE,"E13.3"),sQuery(id+"F0.wireOp",EDGE,"E13.4"),sQuery(id+"F0.wireOp",EDGE,"E13.5"),sQuery(id+"F0.wireOp",EDGE,"E14.0"),sQuery(id+"F0.wireOp",EDGE,"E14.1"),sQuery(id+"F0.wireOp",EDGE,"E14.2"),sQuery(id+"F0.wireOp",EDGE,"E14.3"),sQuery(id+"F0.wireOp",EDGE,"E14.4"),sQuery(id+"F0.wireOp",EDGE,"E14.5"),sQuery(id+"F0.wireOp",EDGE,"E15.0"),sQuery(id+"F0.wireOp",EDGE,"E15.1"),sQuery(id+"F0.wireOp",EDGE,"E15.2"),sQuery(id+"F0.wireOp",EDGE,"E15.3"),sQuery(id+"F0.wireOp",EDGE,"E15.4"),sQuery(id+"F0.wireOp",EDGE,"E15.5"),sQuery(id+"F0.wireOp",EDGE,"E16.0"),sQuery(id+"F0.wireOp",EDGE,"E16.1"),sQuery(id+"F0.wireOp",EDGE,"E16.2"),sQuery(id+"F0.wireOp",EDGE,"E16.3"),sQuery(id+"F0.wireOp",EDGE,"E16.4"),sQuery(id+"F0.wireOp",EDGE,"E16.5"),sQuery(id+"F0.wireOp",EDGE,"E17.0"),sQuery(id+"F0.wireOp",EDGE,"E17.1"),sQuery(id+"F0.wireOp",EDGE,"E17.2"),sQuery(id+"F0.wireOp",EDGE,"E17.3"),sQuery(id+"F0.wireOp",EDGE,"E17.4"),sQuery(id+"F0.wireOp",EDGE,"E17.5"),sQuery(id+"F0.wireOp",EDGE,"E18.0"),sQuery(id+"F0.wireOp",EDGE,"E18.1"),sQuery(id+"F0.wireOp",EDGE,"E18.2"),sQuery(id+"F0.wireOp",EDGE,"E18.3"),sQuery(id+"F0.wireOp",EDGE,"E18.4"),sQuery(id+"F0.wireOp",EDGE,"E18.5"),sQuery(id+"F0.wireOp",EDGE,"E19.bottom"),sQuery(id+"F0.wireOp",EDGE,"E19.top"),sQuery(id+"F0.wireOp",EDGE,"E19.left"),sQuery(id+"F0.wireOp",EDGE,"E19.right")])]});
            hole(context, id + "F8", {"style" : HoleStyle.C_SINK, "endStyle" : HoleEndStyle.THROUGH, "standardTappedOrClearance" : lookupTablePath({ "standard" : "ANSI", "fit" : "Normal (ASME)", "size" : "#10", "type" : "Clearance" }), "standardBlindInLast" : lookupTablePath({ "fit" : "Free", "standard" : "ANSI", "size" : "#10", "type" : "Clearance" }), "holeDiameter" : 5.1 * mm, "cSinkDiameter" : 10.44 * mm, "cSinkAngle" : 82 * degree, "tappedDepth" : 12.7 * mm, "tapClearance" : 3, "locations" : qUnion([Q0]), "scope" : qUnion([Q1])});
        }
        {
            var Q0;
            Q0=qCreatedBy(makeId("Top.planeOp"),FACE);
            var sketch = newSketch(context, id + "F9", { "sketchPlane" : qUnion([Q0])});
            skText(sketch, "E20", { "text": "M3", "fontName": "OpenSans-Regular.ttf"});
            skText(sketch, "E21", { "text": "M4", "fontName": "OpenSans-Regular.ttf"});
            skText(sketch, "E22", { "text": "M5", "fontName": "OpenSans-Regular.ttf"});
            skText(sketch, "E23", { "text": "M6", "fontName": "OpenSans-Regular.ttf"});
            skText(sketch, "E24", { "text": "# 6", "fontName": "OpenSans-Regular.ttf"});
            skText(sketch, "E25", { "text": "# 7", "fontName": "OpenSans-Regular.ttf"});
            skText(sketch, "E26", { "text": "# 8", "fontName": "OpenSans-Regular.ttf"});
            skText(sketch, "E27", { "text": "1", "fontName": "OpenSans-Regular.ttf"});
            skText(sketch, "E28", { "text": "1.5\n", "fontName": "OpenSans-Regular.ttf"});
            skText(sketch, "E29", { "text": "2", "fontName": "OpenSans-Regular.ttf"});
            skText(sketch, "E30", { "text": "2.5", "fontName": "OpenSans-Regular.ttf"});
            skText(sketch, "E31", { "text": "3", "fontName": "OpenSans-Regular.ttf"});
            skText(sketch, "E32", { "text": "4", "fontName": "OpenSans-Regular.ttf"});
            skText(sketch, "E33", { "text": "5", "fontName": "OpenSans-Regular.ttf"});
            skText(sketch, "E34", { "text": "6\n", "fontName": "OpenSans-Regular.ttf"});
            skText(sketch, "E35", { "text": "7", "fontName": "OpenSans-Regular.ttf"});
            skText(sketch, "E36", { "text": "8", "fontName": "OpenSans-Regular.ttf"});
            skText(sketch, "E37", { "text": "9", "fontName": "OpenSans-Regular.ttf"});
            skText(sketch, "E38", { "text": "10", "fontName": "OpenSans-Regular.ttf"});
            const initialGuessF9  = {"E20": [-0.05404, 0.01275, 1, 0, 0.002], "E21": [-0.04544, 0.01275, 1, 0, 0.002], "E22": [-0.03456, 0.01275, 1, 0, 0.002], "E23": [-0.02181, 0.01275, 1, 0, 0.002], "E24": [-0.04915, 0.02813, 1, 0, 0.002], "E25": [-0.03816, 0.02813, 1, 0, 0.002], "E26": [-0.02676, 0.02813, 1, 0, 0.002], "E27": [-0.05803, 0.00338, 1, 0, 0.002], "E28": [-0.05337, 0.00338, 1, 0, 0.002], "E29": [-0.04451, 0.00338, 1, 0, 0.002], "E30": [-0.03888, 0.00338, 1, 0, 0.002], "E31": [-0.0311, 0.00338, 1, 0, 0.002], "E32": [-0.02494, 0.00338, 1, 0, 0.002], "E33": [-0.01805, 0.00338, 1, 0, 0.002], "E34": [-0.01799, -0.00737, 1, 0, 0.002], "E35": [-0.02527, -0.0117, 1, 0, 0.002], "E36": [-0.03393, -0.00424, 1, 0, 0.002], "E37": [-0.04305, -0.01237, 1, 0, 0.002], "E38": [-0.05384, -0.00422, 1, 0, 0.002]};
            skSetInitialGuess(sketch, initialGuessF9);
            skSolve(sketch);
        }
        {
            var Q0;
            Q0 = qSketchRegion(id + "F9", true);
            extrude(context, id + "F10", {"entities" : qUnion([Q0]), "operationType" : NewBodyOperationType.ADD, "depth" : .4 * mm});
        }
    });
